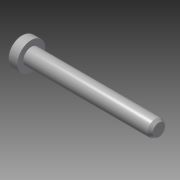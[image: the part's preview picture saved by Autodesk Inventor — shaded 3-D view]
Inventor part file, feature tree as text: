
AUTODESK INVENTOR PART (.ipt)
format: ipt  version: 2014 SP1 (Build 180222100, 222)  size: 103,424 bytes
history: native  units: in
note: dims shown in document units (in); Inventor stores cm internally (conversion verified against a paired STEP export)
features: fillet x1, imported_body x1
ambient origin geometry x8: Origin, YZ Plane, XZ Plane, XY Plane, X Axis, Y Axis, Z Axis, Center Point
bodies: Body1 (feature_tree)
feature tree (2):
  fillet  "Fillet1"  [1 undecoded]
  imported_body  "Base1"
note: 1 required parameter value undecoded (feature->parameter linkage not recoverable at this tier; creation-order binding heuristic only, values carry confidence <= 0.55)
